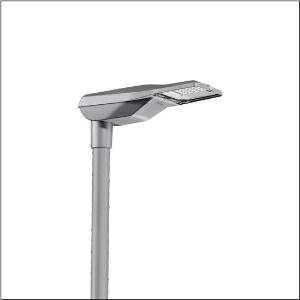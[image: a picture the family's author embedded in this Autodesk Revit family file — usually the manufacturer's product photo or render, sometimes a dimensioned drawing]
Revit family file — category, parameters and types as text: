
# Revit family: streetlight_sl_21_iq_micro___st0_8a_5xe1c21d08cb_82e6
name_source: partatom
category: Lighting Fixtures
units: mm (PartAtom-declared; Revit-internal decimal feet)

## family parameters
Cut with Voids When Loaded = No
Host = Face
Light Source = No
Part Type = Normal
Room Calculation Point = No
Round Connector Dimension = Use Diameter
Shared = No

## types (1)
- --- (1 x LED, 2380 lm, 19.4 W, 2200K)
    Apparent Load = 19 VA
    CIE Flux Codes = 38 75 97 100 100
    Color Rendering = 70
    Color Temperature = 2200K
    Default Elevation = 1800 mm
    Description = Streetlight SL 21 iQ micro, mast luminaire, primary light control with lens, of PMMA, primary optical cover: cover, of toughened safety glass, transparent, light distribution: ST0.8a, light emission: direct distribution, primary light characteristic: asymmetric, installation type: post-top, side-entry, LED, High Power LED, rated luminous flux: 2.380lm, luminous efficacy: 123lm/W, light colour: 722, colour temperature: 2200K, control: Auto-Match, Temp-Guard, Lumen-Switch, Night-Set, Smart-Wire, Light-Fading, Desk-Remote (wireless, voltage-free reading and setting of iQ features in the workshop via application-optimized NFC function/RFID function), optimised constant luminous flux control (CLO 2.0), presetting dimming linear, mains connection: 220..240V, AC, 50/60Hz, start of lifetime: 19W, end of service life: 20W, reduction: 10W, luminaire housing, of diecast aluminium, powder-coated, Siteco® metallic grey (DB 702S), corrosivity category C5 mid according to DIN EN ISO 12944, please order mast flange separately, inclination adjustable: 0°, 5°, 10°, 15°, sealing non-destructively replaceable, multi-level sealing system, length: 528mm, width: 235mm, height: 110mm, mast flange for spigot size: 42mm (side-entry): 5XC10008XM4, 60/48mm (side-entry/post-top): 5XC10108XM2, 76/60mm (side-entry/post-top): 5XC10108XM1, protection rating (complete): IP66, insulation class (complete): insulation class II (safety insulation), certification: CE, ENEC, ENEC+, VDE, impact resistance: IK09, permissible operating ambient temperature for outdoor applications: -40..+50°C, standard-compliant lighting for roads and squares, packaging unit: 1 piece

Light Distribution: ST0.8a
    Height = 110 mm
    Lamp = 1 x LED
    Lamp Light Flux = 2380 lm
    Lamp Power = 19.4 W
    Lamp count = 1
    Length = 528 mm
    Luminous efficacy = 123 lm/W
    Manufacturer = Siteco
    ModVariant = No
    Model = 5XE1C21D08CB
    Number of Poles = 1
    OnlyDefault = Yes
    Power Factor = 1
    Product Name = Streetlight SL 21 iQ micro | ST0.8a
    Product group = mast luminaire | pylon top
    ProductGroupID = 6100
    Protection Class = Protection class II
    Protection Degree = IP 66
    RLX_Detail_Level = 1
    RLX_Emergency_Light_Flux = 0 lm
    RLX_Emergency_Type = 0
    RLX_Emergency_Type_DB = No
    RlxData = <blob elided: 98425 chars, md5=c9517f6d>
    Socket = socket
    Standby Power = 0 W
    System Light Flux = 2380 lm
    System Power = 19 W
    Type Comments = factory setting: luminous flux: 100 % | dim-lin: 254 | 387 mA
    Type Image = l_1006881.jpg
    URL = http://relux.com
    VarID = @adj_069861
    Voltage = 0 V
    Weight = 0.00 kg
    Width = 235 mm

## geometry (parser evidence)
native form markers: Blend x4, Sweep x11
no freeform markers — native parametric forms only
